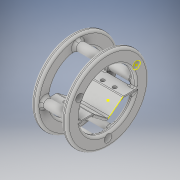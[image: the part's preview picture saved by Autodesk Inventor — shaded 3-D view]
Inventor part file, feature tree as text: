
AUTODESK INVENTOR PART (.ipt)
format: ipt  version: 2019 (Build 230136000, 136)  size: 949,760 bytes
history: native  units: in
note: dims shown in document units (in); Inventor stores cm internally (conversion verified against a paired STEP export)
features: fillet x14, sketch x9, extrude x7, mirror x2, projected_geometry x2, plane x1, pattern_circular x1
ambient origin geometry x8: Origin, YZ Plane, XZ Plane, XY Plane, X Axis, Y Axis, Z Axis, Center Point
bodies: Solid1 (feature_tree)
feature tree (36):
  extrude  "Extrusion1"  Depth=0.4331in
  extrude  "Extrusion2"  Depth=0.5118in
  mirror  "Mirror1"
  extrude  "Extrusion3"  Depth=0.3603in
  plane  "Work Plane1"
  extrude  "Extrusion4"  Depth=0.1181in
  extrude  "Extrusion5"  Depth=1.1811in TaperAngle=0.0deg
  pattern_circular  "Circular Pattern1"  Count=3  [1 undecoded]
  extrude  "Extrusion6"  Depth=0.1969in TaperAngle=0.0deg
  extrude  "Extrusion7"  Depth=0.2441in
  mirror  "Mirror2"
  sketch  "Sketch12"  dims[d53=0.122in]
  sketch  "Sketch14"  dims[d55=0.0787in d56=0.0787in d57=0.0591in d58=0.0787in d59=0.0787in d60=0.0787in d61=0.0787in d62=0.0787in d63=0.0787in d64=0.1969in d65=0.0591in d66=0.0591in d67=0.0591in d68=0.0591in d69=0.0591in]
  fillet  "Fillet2"  Radius=0.7874in
  fillet  "Fillet3"  Radius=1.1811in
  fillet  "Fillet4"  Radius=2.1654in
  fillet  "Fillet5"  Radius=0.2756in
  fillet  "Fillet6"  Radius=0.1969in
  fillet  "Fillet7"  Radius=0.1969in
  fillet  "Fillet8"  Radius=0.2756in
  fillet  "Fillet9"  Radius=0.2756in
  fillet  "Fillet10"  Radius=1.1811in
  fillet  "Fillet11"  Radius=0.122in
  fillet  "Fillet12"  Radius=0.1969in
  fillet  "Fillet13"  Radius=0.4724in
  fillet  "Fillet14"  Radius=0.0787in
  fillet  "Fillet15"  [1 undecoded]
  sketch  "Sketch2"  dims[d4=2.7165in d5=0.4331in]
  sketch  "Sketch4"  dims[d6=0.1969in d7=0.0in d16=0.5118in]
  sketch  "Sketch5"  dims[d17=0.5118in d18=0.3603in]
  projected_geometry  "Projected Loop1"
  sketch  "Sketch6"  dims[d20=0.1181in d21=0.1181in]
  projected_geometry  "Projected Loop2"
  sketch  "Sketch9"  dims[d22=180.0deg d23=1.1811in d24=0.0in d25=1.1811in d26=0.0in]
  sketch  "Sketch10"  dims[d27=-1.1811in d28=0.1969in d29=0.0in]
  sketch  "Sketch11"  dims[d32=2.1654in d33=0.2441in d34=0.7874in d35=0.0in d36=1.1811in d37=360.0deg d39=2.1654in d40=0.2756in d41=0.1969in d42=0.1969in d43=0.2756in d44=0.2756in d45=1.1811in d46=0.0in d47=0.122in d48=0.1969in d49=0.0in d50=0.4724in d51=0.0787in d52=90.0deg]
note: 2 required parameter values undecoded (feature->parameter linkage not recoverable at this tier; creation-order binding heuristic only, values carry confidence <= 0.55)
